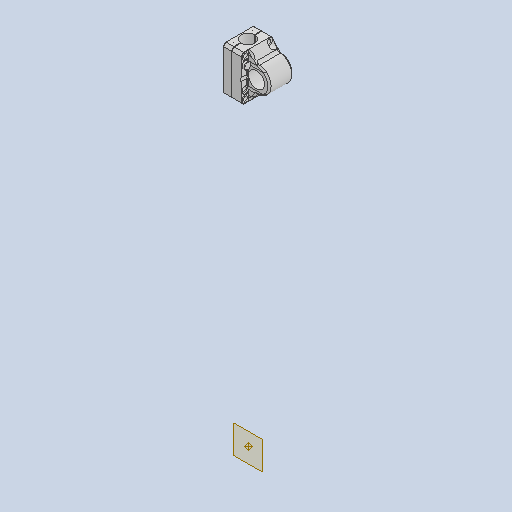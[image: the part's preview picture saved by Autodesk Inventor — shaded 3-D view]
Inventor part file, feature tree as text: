
AUTODESK INVENTOR PART (.ipt)
format: ipt  version: 2024.1 (Build 281209000, 209)  size: 416,256 bytes
history: native  units: mm
features: other x9, sketch x9, plane x2
ambient origin geometry x8: Origin, YZ Plane, XZ Plane, XY Plane, X Axis, Y Axis, Z Axis, Center Point
bodies: Body1 (feature_tree), Body2 (feature_tree), Body3 (feature_tree)
feature tree (20):
  other  "rack-mounts.ipt"
  other  "clamp-top::rack-mounts.ipt"
  other  "screw-cap::rack-mounts.ipt"
  other  "clamp-base::rack-mounts.ipt"
  other  "TaggingFeature1"
  sketch  "Sketch3"  dims[d0=10.0mm]
  sketch  "Sketch4"
  sketch  "Sketch5"
  sketch  "Sketch6"
  sketch  "Sketch7"
  sketch  "Sketch9"
  sketch  "Sketch10"
  sketch  "Sketch11"
  sketch  "Sketch12"
  plane  "Work Plane1"
  plane  "Work Plane2"
  other  "Work Point1"
  other  "clamp-top"
  other  "screw-cap"
  other  "clamp-base"
